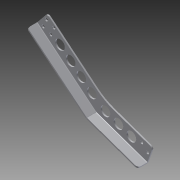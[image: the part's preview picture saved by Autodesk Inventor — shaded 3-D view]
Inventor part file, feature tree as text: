
AUTODESK INVENTOR PART (.ipt)
format: ipt  version: 2014 SP1 (Build 180222100, 222)  size: 293,376 bytes
history: native  units: in
note: dims shown in document units (in); Inventor stores cm internally (conversion verified against a paired STEP export)
features: reference x5, sheet_metal_op x3, chamfer x2, other x2, sketch x1
ambient origin geometry x8: Origin, YZ Plane, XZ Plane, XY Plane, X Axis, Y Axis, Z Axis, Center Point
bodies: Solid1 (feature_tree)
feature tree (13):
  sketch  "Sketch1"  dims[d5=0.125in d51=5.0in d53=0.25in d59=0.2216in d60=0.25in d67=1.0994in d70=0.25in d72=1.375in d73=1.375in d74=0.2216in d75=0.9318in d76=1.0in d77=1.0in d78=0.1in d80=0.1in d81=0.125in d82=0.0625in d83=0.25in d84=0.125in d85=90.0deg d86=0.05in d87=0.125in d88=0.0625in d89=0.25in d90=0.125in d91=90.0deg d92=0.05in d93=0.5in d94=0.1in d95=0.5in d96=6.9469in d97=4.9278in d98=2.3622in d100=1.0894in d101=0.3937in d103=1.0in d105=0.5in d106=0.1in d107=0.5in d108=1.9685in d110=0.857in d111=0.3937in d113=1.0in d115=0.25in d116=0.875in d117=1.0in d118=1.5748in d120=1.25in d121=0.3937in d123=1.0in d125=0.875in d126=0.5in d127=1.1811in d129=1.25in d130=0.3937in d132=1.0in]
  sheet_metal_op  "Face1"
  chamfer  "Corner Round2"
  sheet_metal_op  "Fold2"
  sheet_metal_op  "Fold3"
  chamfer  "Corner Round3"
  reference  "Reference5"
  reference  "Reference6"
  other  "Plate1"
  reference  "Reference7"
  reference  "Reference8"
  reference  "Reference9"
  other  "Definition1"
